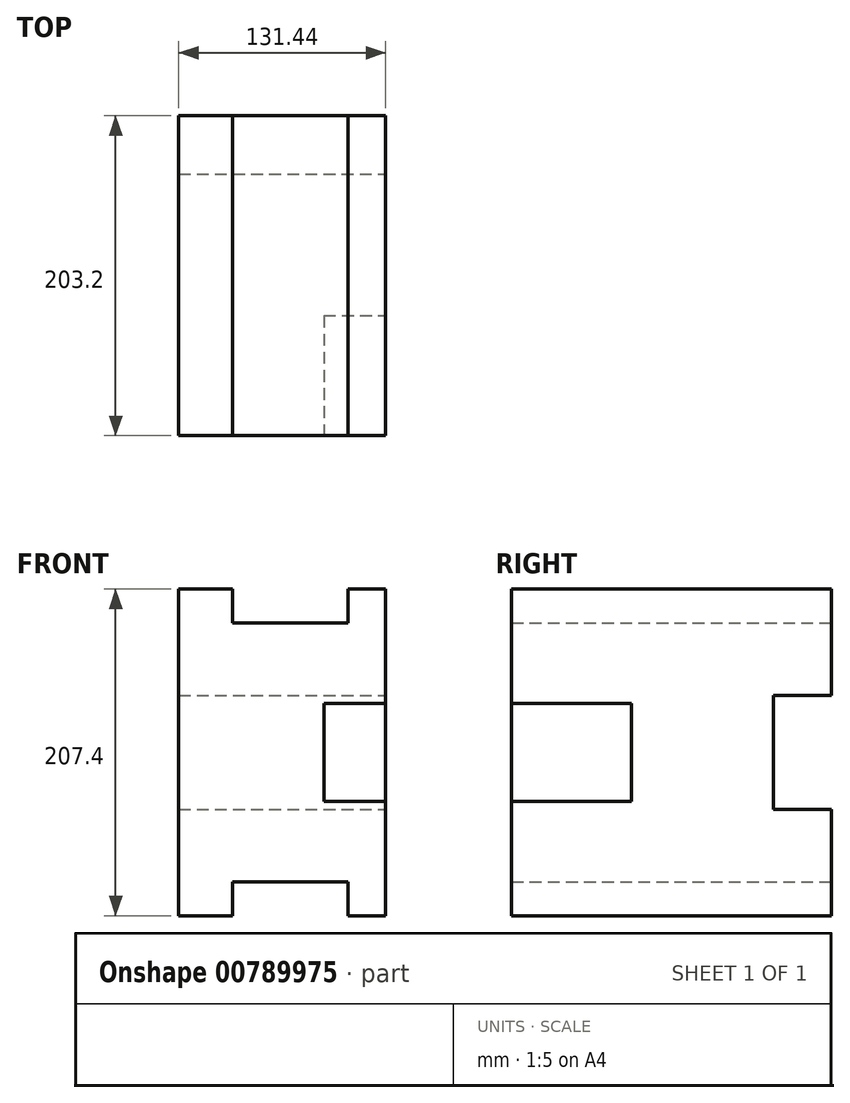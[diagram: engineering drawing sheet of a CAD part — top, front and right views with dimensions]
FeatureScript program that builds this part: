
annotation { "Feature Type Name" : "Feature", "Feature Type Description" : "" }
export const myFeature = defineFeature(function(context is Context, id is Id, definition is map)
    precondition{}
    {
        {
            var Q0;
            Q0=qCreatedBy(makeId("Front.planeOp"),FACE);
            var sketch = newSketch(context, id + "F0", { "sketchPlane" : qUnion([Q0])});
            skLineSegment(sketch, "E0.top", {"start": v(-61.63, 103.7) * mm, "end": v(69.81, 103.7) * mm});
            skLineSegment(sketch, "E0.left", {"start": v(-61.63, 0) * mm, "end": v(-61.63, 103.7) * mm});
            skLineSegment(sketch, "E0.right", {"start": v(69.81, 0) * mm, "end": v(69.81, 103.7) * mm});
            skLineSegment(sketch, "E1", {"start": v(-27.56, 0) * mm, "end": v(-27.56, 21.35) * mm});
            skLineSegment(sketch, "E2", {"start": v(-27.56, 21.35) * mm, "end": v(46, 21.35) * mm});
            skLineSegment(sketch, "E3", {"start": v(46, 21.35) * mm, "end": v(46, 0) * mm});
            skLineSegment(sketch, "E4", {"start": v(-61.63, 0) * mm, "end": v(-27.56, 0) * mm});
            skLineSegment(sketch, "E5", {"start": v(46, 0) * mm, "end": v(69.81, 0) * mm});
            skSolve(sketch);
        }
        {
            var Q0;
            Q0=makeQuery(id+"F0.imprint","IMPRINT",FACE,{"disambiguationData":[TD([[makeQuery(id+"F0.imprint","IMPRINT",EDGE,{"derivedFrom":sQuery(id+"F0.wireOp",EDGE,"E0.top")}),-1.0]])]});
            extrude(context, id + "F1", {"entities" : qUnion([Q0]), "depth" : 203.2 * mm, "offsetDistance" : 25.4 * mm});
        }
        {
            var Q0;
            Q0=makeQuery(id+"F1.opExtrude","CAP_FACE",FACE,{"disambiguationData":[OSD([sQuery(id+"F0.wireOp",EDGE,"E0.top"),sQuery(id+"F0.wireOp",EDGE,"E0.left"),sQuery(id+"F0.wireOp",EDGE,"E0.right"),sQuery(id+"F0.wireOp",EDGE,"E1"),sQuery(id+"F0.wireOp",EDGE,"E2"),sQuery(id+"F0.wireOp",EDGE,"E3"),sQuery(id+"F0.wireOp",EDGE,"E4"),sQuery(id+"F0.wireOp",EDGE,"E5")])],"isStart":false});
            var sketch = newSketch(context, id + "F2", { "sketchPlane" : qUnion([Q0])});
            skLineSegment(sketch, "E6", {"start": v(69.81, 103.7) * mm, "end": v(30.58, 103.7) * mm});
            skLineSegment(sketch, "E7", {"start": v(30.58, 103.7) * mm, "end": v(30.58, 72.51) * mm});
            skLineSegment(sketch, "E8", {"start": v(30.58, 72.51) * mm, "end": v(69.81, 72.51) * mm});
            skLineSegment(sketch, "E9", {"start": v(69.81, 72.51) * mm, "end": v(69.81, 103.7) * mm});
            skSolve(sketch);
        }
        {
            var Q0;
            Q0=makeQuery(id+"F2.imprint","IMPRINT",FACE,{"disambiguationData":[TD([[makeQuery(id+"F2.imprint","IMPRINT",EDGE,{"derivedFrom":sQuery(id+"F2.wireOp",EDGE,"E6")}),-1.0]])]});
            extrude(context, id + "F3", {"entities" : qUnion([Q0]), "operationType" : NewBodyOperationType.REMOVE, "oppositeDirection" : true, "depth" : 76.2 * mm, "offsetDistance" : 25.4 * mm});
        }
        {
            var Q0;
            Q0=makeQuery(id+"F1.opExtrude","SWEPT_FACE",FACE,{"disambiguationData":[OSD([sQuery(id+"F0.wireOp",EDGE,"E0.right")])]});
            var sketch = newSketch(context, id + "F4", { "sketchPlane" : qUnion([Q0])});
            skLineSegment(sketch, "E10", {"start": v(0, 103.7) * mm, "end": v(-36.94, 103.7) * mm});
            skLineSegment(sketch, "E11", {"start": v(-36.94, 103.7) * mm, "end": v(-36.94, 67.6) * mm});
            skLineSegment(sketch, "E12", {"start": v(-36.94, 67.6) * mm, "end": v(0, 67.6) * mm});
            skLineSegment(sketch, "E13", {"start": v(0, 67.6) * mm, "end": v(0, 103.7) * mm});
            skSolve(sketch);
        }
        {
            var Q0;
            Q0 = qSketchRegion(id + "F4", true);
            var Q1;
            Q1=makeQuery(id+"F4.imprint","IMPRINT",FACE,{"disambiguationData":[TD([[makeQuery(id+"F4.imprint","IMPRINT",EDGE,{"derivedFrom":sQuery(id+"F4.wireOp",EDGE,"E10")}),-1.0]])]});
            extrude(context, id + "F5", {"entities" : qUnion([Q0, Q1]), "operationType" : NewBodyOperationType.REMOVE, "oppositeDirection" : true, "depth" : 152.4 * mm, "offsetDistance" : 25.4 * mm});
        }
        {
            var Q0;
            Q0=makeQuery(id+"F1.opExtrude","SWEPT_BODY",BODY,{"disambiguationData":[OSD([sQuery(id+"F0.wireOp",EDGE,"E0.top"),sQuery(id+"F0.wireOp",EDGE,"E0.left"),sQuery(id+"F0.wireOp",EDGE,"E0.right"),sQuery(id+"F0.wireOp",EDGE,"E1"),sQuery(id+"F0.wireOp",EDGE,"E2"),sQuery(id+"F0.wireOp",EDGE,"E3"),sQuery(id+"F0.wireOp",EDGE,"E4"),sQuery(id+"F0.wireOp",EDGE,"E5")])]});
            var Q1;
            Q1=makeQuery(id+"F1.opExtrude","SWEPT_FACE",FACE,{"disambiguationData":[OSD([sQuery(id+"F0.wireOp",EDGE,"E0.top")])]});
            mirror(context, id + "F6", {"operationType" : NewBodyOperationType.ADD, "entities" : qUnion([Q0]), "mirrorPlane" : qUnion([Q1])});
        }
    });
